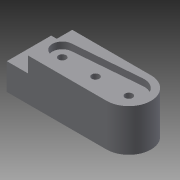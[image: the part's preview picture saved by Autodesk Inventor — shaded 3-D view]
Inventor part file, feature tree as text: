
AUTODESK INVENTOR PART (.ipt)
format: ipt  version: 2015 (Build 190159000, 159)  size: 127,488 bytes
history: native  units: in
note: dims shown in document units (in); Inventor stores cm internally (conversion verified against a paired STEP export)
features: extrude x4
ambient origin geometry x8: Origin, YZ Plane, XZ Plane, XY Plane, X Axis, Y Axis, Z Axis, Center Point
bodies: Body1 (feature_tree)
feature tree (4):
  extrude  "Extrusion4"  Depth=0.6299in
  extrude  "Extrusion5"  Depth=1.1811in
  extrude  "Extrusion6"  Depth=0.1575in
  extrude  "Extrusion7"  Depth=1.9685in
